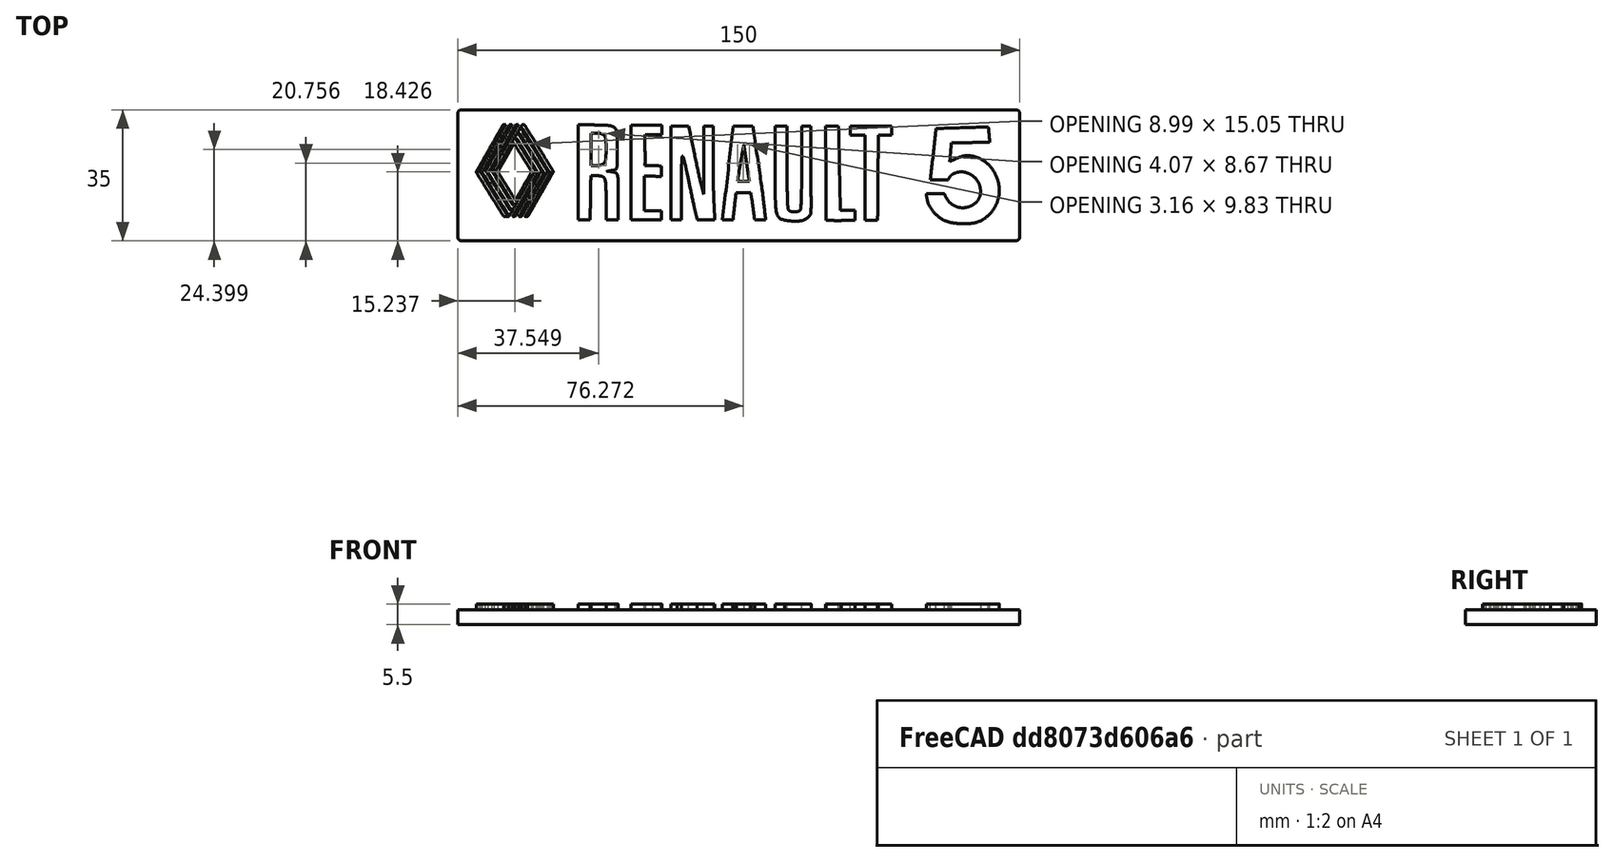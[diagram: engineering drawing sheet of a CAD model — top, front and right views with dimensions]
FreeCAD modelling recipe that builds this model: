
FCSTD DOCUMENT  (FreeCAD 0.16R6712 (Git))
Label: Renault 5
License: All rights reserved
LicenseURL: http://en.wikipedia.org/wiki/All_rights_reserved
objects: Part::Feature×12, Part::Extrusion×11, Part::FeaturePython×2, Part::Cut×2, Part::Box×1, Part::Fillet×1
note: 29 computed .brp shape members not serialized (recipe doc carries the construction recipe); baked Part::Feature solids carry a one-line shape summary decoded from their .brp

FEATURE [Part::Feature] path4158  label="5"
  Placement = pos=(-22,62,0) rot=(0,0,-1;0.029671rad)
  shape: bbox 17.05 x 22.39 x 2e-07 mm, 0 faces, 0 solids (baked)
FEATURE [Part::Feature] path4138  label="Rombo Ext"
  shape: bbox 229.2 x 272.4 x 2e-07 mm, 0 faces, 0 solids (baked)
FEATURE [Part::Feature] path4138001  label="Rombo Int"
  shape: bbox 99.9 x 167.2 x 2e-07 mm, 0 faces, 0 solids (baked)
FEATURE [Part::Feature] path4140
  Placement = pos=(30,2,0) rot=(0,0,1;0rad)
  shape: bbox 9.814 x 25.67 x 2e-07 mm, 0 faces, 0 solids (baked)
FEATURE [Part::Feature] path4140001
  Placement = pos=(30,2,0) rot=(0,0,1;0rad)
  shape: bbox 7.87 x 25.27 x 2e-07 mm, 0 faces, 0 solids (baked)
FEATURE [Part::Feature] path4140002
  Placement = pos=(30,2,0) rot=(0,0,1;0rad)
  shape: bbox 10.94 x 25.22 x 2e-07 mm, 0 faces, 0 solids (baked)
FEATURE [Part::Feature] path4140003
  Placement = pos=(30,2,0) rot=(0,0,1;0rad)
  shape: bbox 10.83 x 25.46 x 2e-07 mm, 0 faces, 0 solids (baked)
FEATURE [Part::Feature] path4140004
  Placement = pos=(30,2,0) rot=(0,0,1;0rad)
  shape: bbox 4.093 x 8.704 x 2e-07 mm, 0 faces, 0 solids (baked)
FEATURE [Part::Feature] path4140005
  Placement = pos=(30,2,0) rot=(0,0,1;0rad)
  shape: bbox 8.199 x 25.34 x 2e-07 mm, 0 faces, 0 solids (baked)
FEATURE [Part::Feature] path4140006
  Placement = pos=(30,2,0) rot=(0,0,1;0rad)
  shape: bbox 11.75 x 25.05 x 2e-07 mm, 0 faces, 0 solids (baked)
FEATURE [Part::Feature] path4140007
  Placement = pos=(30,2,0) rot=(0,0,1;0rad)
  shape: bbox 11.57 x 25.13 x 2e-07 mm, 0 faces, 0 solids (baked)
FEATURE [Part::Feature] path4140008
  Placement = pos=(30,2,0) rot=(0,0,1;0rad)
  shape: bbox 3.163 x 9.829 x 2e-07 mm, 0 faces, 0 solids (baked)
FEATURE [Part::Box] Box  label="Cube"
  Height = 4
  Length = 150
  Placement = pos=(1,-29,-4) rot=(0,0,1;0rad)
  Width = 35
FEATURE [Part::FeaturePython] Scale  label="Rombo"  # Draft clone (typed FeaturePython)
  Objects = -> [path4138001,path4138]
  Placement = pos=(2,4,0) rot=(0,0,1;0rad)
  Scale = (0.09,0.09,0.09)
FEATURE [Part::FeaturePython] Scale001  # Draft clone (typed FeaturePython)
  Objects = -> [path4158]
  Placement = pos=(-42.4022,60,0) rot=(0,0,1;0rad)
  Scale = (1.15,1.15,1)
FEATURE [Part::Extrusion] Extrude
  Base = -> path4140
  Dir = (0,0,1.5)
  Solid = true
FEATURE [Part::Extrusion] Extrude001
  Base = -> path4140001
  Dir = (0,0,1.5)
  Solid = true
FEATURE [Part::Extrusion] Extrude002
  Base = -> path4140002
  Dir = (0,0,1.5)
  Solid = true
FEATURE [Part::Extrusion] Extrude003
  Base = -> path4140003
  Dir = (0,0,1.5)
  Solid = true
FEATURE [Part::Extrusion] Extrude004
  Base = -> path4140004
  Dir = (0,0,1.5)
  Solid = true
FEATURE [Part::Extrusion] Extrude005
  Base = -> path4140005
  Dir = (0,0,1.5)
  Solid = true
FEATURE [Part::Extrusion] Extrude006
  Base = -> path4140006
  Dir = (0,0,1.5)
  Solid = true
FEATURE [Part::Extrusion] Extrude007
  Base = -> path4140007
  Dir = (0,0,1.5)
  Solid = true
FEATURE [Part::Extrusion] Extrude008
  Base = -> path4140008
  Dir = (0,0,1.5)
  Solid = true
FEATURE [Part::Extrusion] Extrude009
  Base = -> Scale
  Dir = (0,0,1.5)
  Solid = true
FEATURE [Part::Extrusion] Extrude010
  Base = -> Scale001
  Dir = (0,0,1.5)
  Solid = true
FEATURE [Part::Fillet] Fillet
  Base = -> Box
  Edges = 4 edges r=1: [Edge1,Edge3,Edge5,Edge7]
FEATURE [Part::Cut] Cut
  Base = -> Extrude003
  Tool = -> Extrude004
FEATURE [Part::Cut] Cut001
  Base = -> Extrude007
  Tool = -> Extrude008
